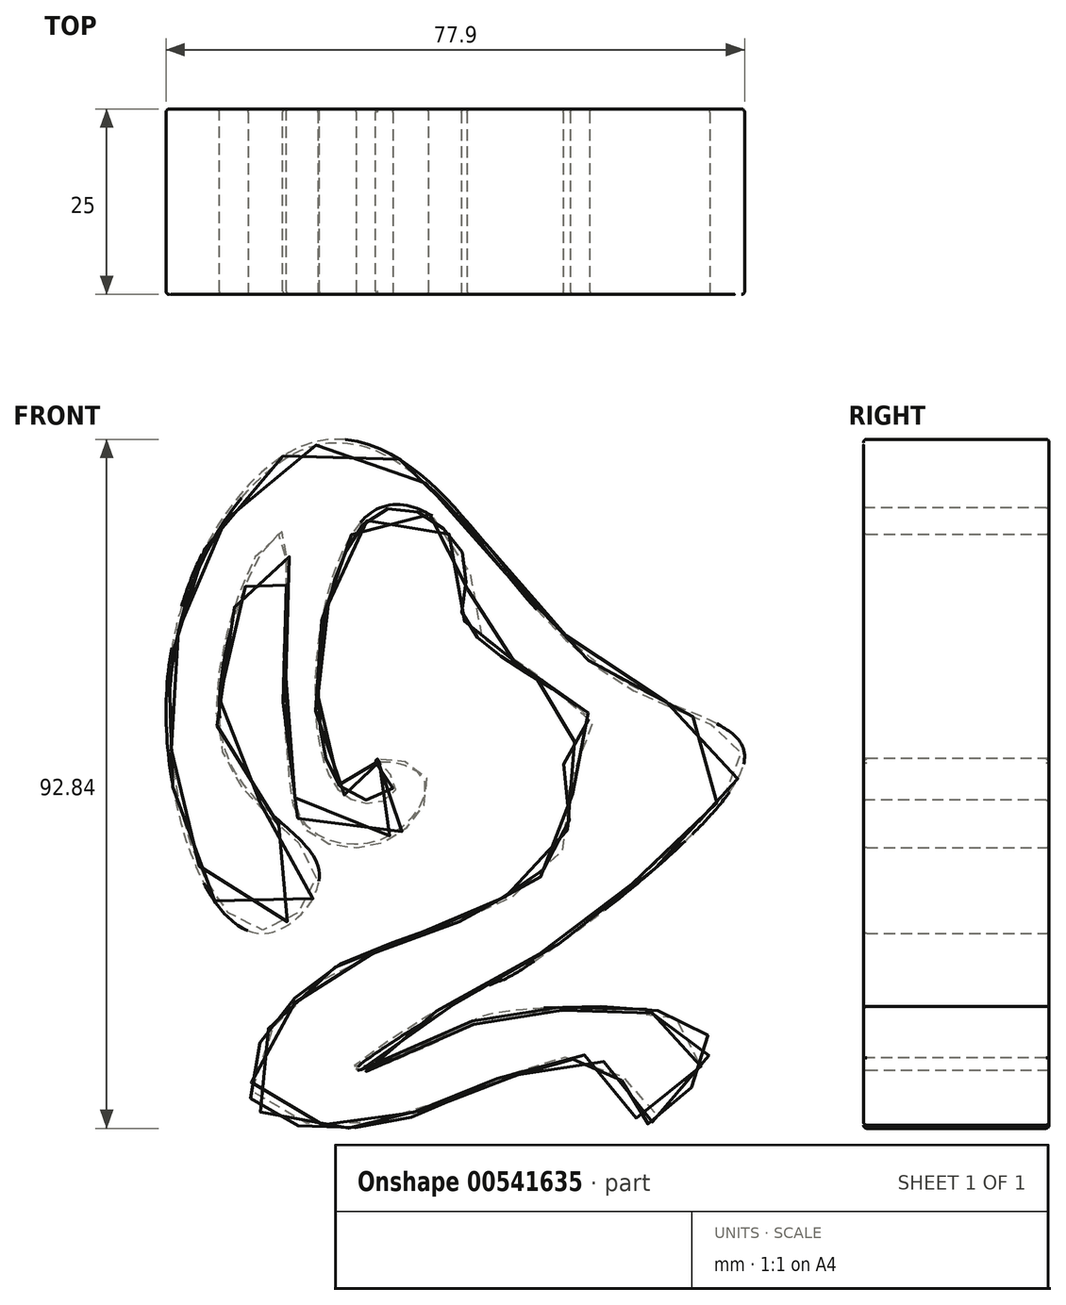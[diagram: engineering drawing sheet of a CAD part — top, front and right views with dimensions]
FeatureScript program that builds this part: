
annotation { "Feature Type Name" : "Feature", "Feature Type Description" : "" }
export const myFeature = defineFeature(function(context is Context, id is Id, definition is map)
    precondition{}
    {
        {
            var Q0;
            Q0=qCreatedBy(makeId("Front.planeOp"),FACE);
            var sketch = newSketch(context, id + "F0", { "sketchPlane" : qUnion([Q0])});
            skFitSpline(sketch, "E0", {"points": [v(-35.88, 49.08) * mm, v(-33.58, 45.55) * mm, v(-40.4, 45.27) * mm, v(-35.88, 82.38) * mm, v(-23.74, 75.79) * mm, v(-23.74, 67.47) * mm, v(-7.1, 54.29) * mm, v(-10.23, 50.58) * mm, v(-9.8, 44.49) * mm, v(-14.14, 33.61) * mm, v(-38.5, 22.73) * mm, v(-44.16, 19.25) * mm, v(-50.25, 13.16) * mm, v(-51.99, 2.29) * mm, v(-35.02, 0) * mm, v(-29.37, 1.85) * mm, v(-15.88, 7.07) * mm, v(-5.87, 8.8) * mm, v(-2.4, 4.9) * mm, v(0, 0) * mm, v(8.91, 11.85) * mm, v(-18.06, 15.33) * mm, v(-23.7, 13.6) * mm, v(-38.5, 7.5) * mm, v(-20.66, 18.82) * mm, v(-17.63, 20.12) * mm, v(13.7, 48.84) * mm, v(-2.4, 59.72) * mm, v(-28.6, 86.54) * mm, v(-45.94, 91.4) * mm, v(-63.98, 59.49) * mm, v(-51.84, 25.85) * mm, v(-43.52, 34.17) * mm, v(-56.34, 51.16) * mm, v(-49.06, 79.6) * mm, v(-48.37, 62.6) * mm, v(-47.67, 48.04) * mm, v(-45.25, 39.72) * mm, v(-34.07, 38.44) * mm, v(-29.35, 47.28) * mm, v(-35.88, 49.08) * mm]});
            skSolve(sketch);
        }
        {
            var Q0;
            Q0 = qSketchRegion(id + "F0", true);
            extrude(context, id + "F1", {"entities" : qUnion([Q0]), "depth" : 25 * mm, "offsetDistance" : 25 * mm});
        }
        {
            var Q0;
            Q0=makeQuery(id+"F1.opExtrude","CAP_EDGE",EDGE,{"disambiguationData":[OSD([sQuery(id+"F0.wireOp",EDGE,"E0")])],"isStart":false});
            var Q1;
            Q1=makeQuery(id+"F1.opExtrude","CAP_EDGE",EDGE,{"disambiguationData":[OSD([sQuery(id+"F0.wireOp",EDGE,"E0")])],"isStart":true});
            fillet(context, id + "F2", {"entities" : qUnion([Q0, Q1]), "tangentPropagation" : true, "radius" : .44 * mm, "defaultsChanged" : true, "vertexSettings" : [], "allowEdgeOverflow" : false});
        }
    });
